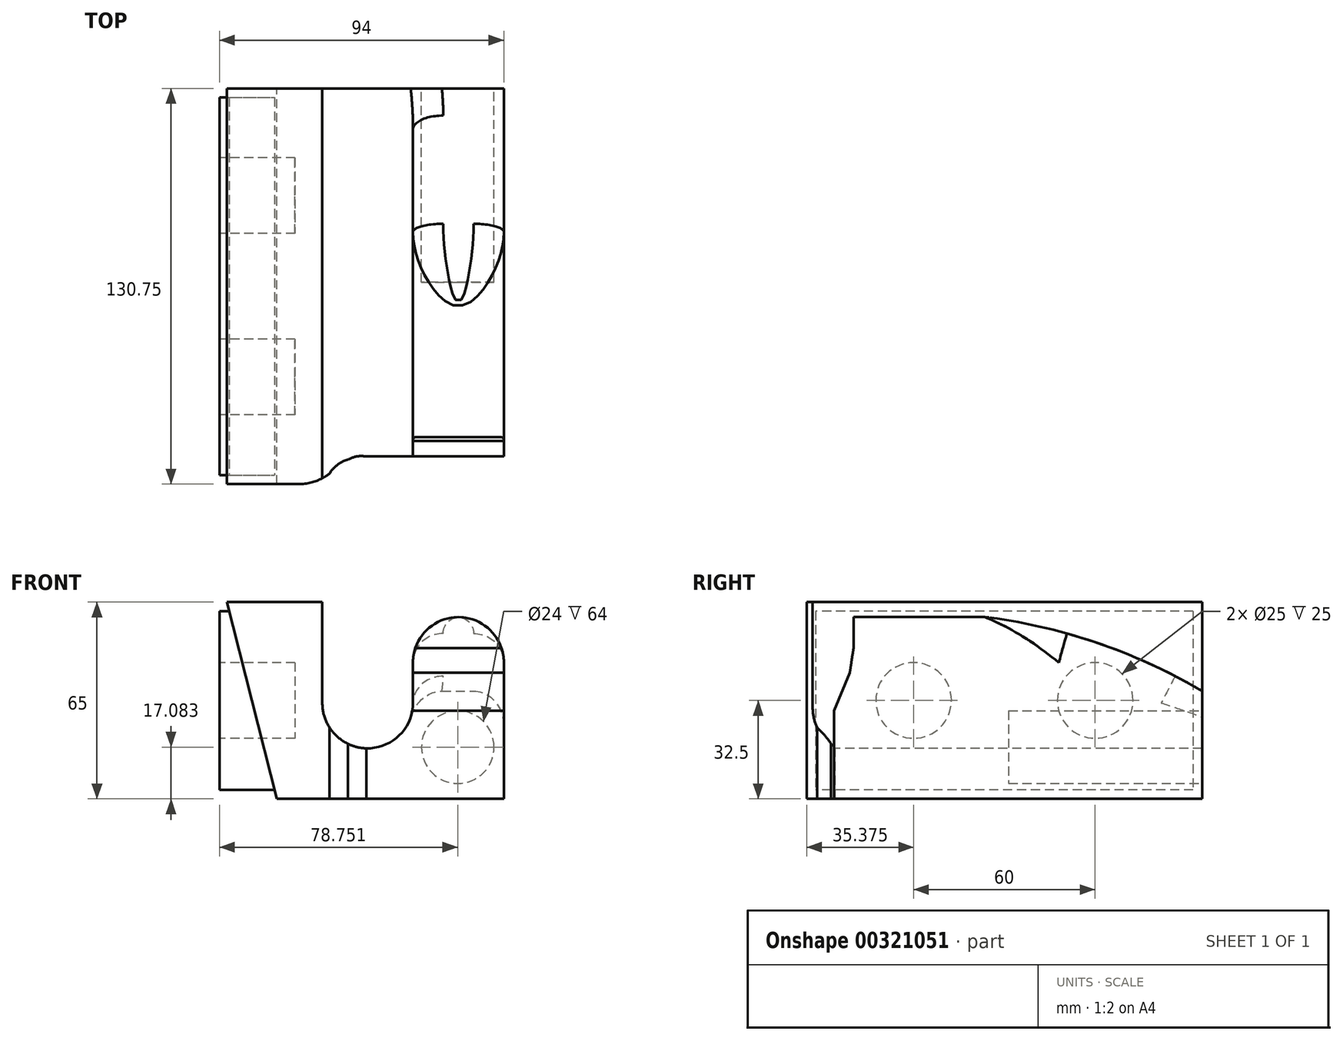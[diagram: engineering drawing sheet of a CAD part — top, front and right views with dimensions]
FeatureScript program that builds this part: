
annotation { "Feature Type Name" : "Feature", "Feature Type Description" : "" }
export const myFeature = defineFeature(function(context is Context, id is Id, definition is map)
    precondition{}
    {
        {
            var Q0;
            Q0=qCreatedBy(makeId("Front.planeOp"),FACE);
            var sketch = newSketch(context, id + "F0", { "sketchPlane" : qUnion([Q0])});
            skLineSegment(sketch, "E0.bottom", {"start": v(37.5, 32.5) * mm, "end": v(-37.5, 32.5) * mm});
            skLineSegment(sketch, "E0.top", {"start": v(37.5, -32.5) * mm, "end": v(-37.5, -32.5) * mm});
            skLineSegment(sketch, "E0.left", {"start": v(37.5, 32.5) * mm, "end": v(37.5, -32.5) * mm});
            skLineSegment(sketch, "E0.right", {"start": v(-37.5, 32.5) * mm, "end": v(-37.5, -32.5) * mm});
            skPoint(sketch, "E0.middle", {"position": v(0, 0) * mm});
            skLineSegment(sketch, "E1", {"start": v(-37.5, 32.5) * mm, "end": v(-54.03, 32.5) * mm});
            skLineSegment(sketch, "E2", {"start": v(-54.03, 32.5) * mm, "end": v(-37.5, -32.5) * mm});
            skSolve(sketch);
        }
        {
            var Q0;
            Q0 = qSketchRegion(id + "F0", true);
            extrude(context, id + "F1", {"entities" : qUnion([Q0]), "depth" : 130.75 * mm});
        }
        {
            var Q0;
            Q0=makeQuery(id+"F1.opExtrude","CAP_FACE",FACE,{"disambiguationData":[OSD([sQuery(id+"F0.wireOp",EDGE,"E0.bottom"),sQuery(id+"F0.wireOp",EDGE,"E0.top"),sQuery(id+"F0.wireOp",EDGE,"E0.left"),sQuery(id+"F0.wireOp",EDGE,"E1"),sQuery(id+"F0.wireOp",EDGE,"E2")])],"isStart":false});
            var sketch = newSketch(context, id + "F2", { "sketchPlane" : qUnion([Q0])});
            skLineSegment(sketch, "E3", {"start": v(37.5, -32.5) * mm, "end": v(37.5, 12.5) * mm});
            skArc(sketch, "E4", {"start": v(37.5, 12.5) * mm, "mid": v(22.47, 27.53) * mm, "end": v(7.45, 12.5) * mm});
            skLineSegment(sketch, "E5", {"start": v(7.45, 12.5) * mm, "end": v(7.45, -0.85) * mm});
            skArc(sketch, "E6", {"start": v(-22.5, -0.85) * mm, "mid": v(-7.53, -15.82) * mm, "end": v(7.45, -0.85) * mm});
            skLineSegment(sketch, "E7", {"start": v(-22.5, -0.85) * mm, "end": v(-22.5, 32.5) * mm});
            skLineSegment(sketch, "E8", {"start": v(-22.5, 32.5) * mm, "end": v(37.5, 32.5) * mm});
            skLineSegment(sketch, "E9", {"start": v(37.5, 32.5) * mm, "end": v(37.5, 12.5) * mm});
            skSolve(sketch);
        }
        {
            var Q0;
            Q0 = qSketchRegion(id + "F2", true);
            extrude(context, id + "F3", {"entities" : qUnion([Q0]), "operationType" : NewBodyOperationType.REMOVE, "oppositeDirection" : true, "depth" : 200 * mm});
        }
        {
            var Q0;
            Q0=makeQuery(id+"F1.opExtrude","SWEPT_FACE",FACE,{"disambiguationData":[OSD([sQuery(id+"F0.wireOp",EDGE,"E0.top")])]});
            var sketch = newSketch(context, id + "F4", { "sketchPlane" : qUnion([Q0])});
            skLineSegment(sketch, "E10", {"start": v(-37.5, 130.75) * mm, "end": v(-30.22, 130.75) * mm});
            skArc(sketch, "E11", {"start": v(-20.1, 127.25) * mm, "mid": v(-24.87, 129.85) * mm, "end": v(-30.22, 130.75) * mm});
            skArc(sketch, "E12", {"start": v(-20.1, 127.25) * mm, "mid": v(-17.49, 124.36) * mm, "end": v(-13.98, 122.65) * mm});
            skArc(sketch, "E13", {"start": v(-13.98, 122.65) * mm, "mid": v(-11.07, 121.6) * mm, "end": v(-7.96, 121.63) * mm});
            skLineSegment(sketch, "E14", {"start": v(-7.96, 121.63) * mm, "end": v(37.5, 121.63) * mm});
            skLineSegment(sketch, "E15", {"start": v(37.5, 121.63) * mm, "end": v(37.5, 130.75) * mm});
            skLineSegment(sketch, "E16", {"start": v(37.5, 130.75) * mm, "end": v(-30.22, 130.75) * mm});
            skSolve(sketch);
        }
        {
            var Q0;
            Q0 = qSketchRegion(id + "F4", true);
            extrude(context, id + "F5", {"entities" : qUnion([Q0]), "operationType" : NewBodyOperationType.REMOVE, "oppositeDirection" : true, "depth" : 200 * mm});
        }
        {
            var Q0;
            Q0=makeQuery(id+"F1.opExtrude","SWEPT_FACE",FACE,{"disambiguationData":[OSD([sQuery(id+"F0.wireOp",EDGE,"E0.left")])]});
            var sketch = newSketch(context, id + "F6", { "sketchPlane" : qUnion([Q0])});
            skLineSegment(sketch, "E17", {"start": v(-121.63, -3.42) * mm, "end": v(-116.52, 9.21) * mm});
            skLineSegment(sketch, "E18", {"start": v(-116.52, 9.21) * mm, "end": v(-115.21, 17.34) * mm});
            skLineSegment(sketch, "E19", {"start": v(-115.21, 17.34) * mm, "end": v(-115.21, 28.67) * mm});
            skLineSegment(sketch, "E20", {"start": v(-115.21, 28.67) * mm, "end": v(-121.63, 28.67) * mm});
            skLineSegment(sketch, "E21", {"start": v(-121.63, 28.67) * mm, "end": v(-121.63, -3.42) * mm});
            skSolve(sketch);
        }
        {
            var Q0;
            Q0 = qSketchRegion(id + "F6", true);
            extrude(context, id + "F7", {"entities" : qUnion([Q0]), "operationType" : NewBodyOperationType.REMOVE, "oppositeDirection" : true, "depth" : 34 * mm});
        }
        {
            var Q0;
            Q0=makeQuery(id+"F1.opExtrude","SWEPT_FACE",FACE,{"disambiguationData":[OSD([sQuery(id+"F0.wireOp",EDGE,"E0.left")])]});
            var sketch = newSketch(context, id + "F8", { "sketchPlane" : qUnion([Q0])});
            skArc(sketch, "E22", {"start": v(0, 3.08) * mm, "mid": v(-42.78, 21.58) * mm, "end": v(-88.8, 28.97) * mm});
            skLineSegment(sketch, "E23", {"start": v(0, 3.08) * mm, "end": v(7.52, 3.08) * mm});
            skLineSegment(sketch, "E24", {"start": v(7.52, 3.08) * mm, "end": v(5.36, 33) * mm});
            skLineSegment(sketch, "E25", {"start": v(5.36, 33) * mm, "end": v(-104, 28.9) * mm});
            skLineSegment(sketch, "E26", {"start": v(-104, 28.9) * mm, "end": v(-88.8, 28.97) * mm});
            skSolve(sketch);
        }
        {
            var Q0;
            Q0 = qSketchRegion(id + "F8", true);
            extrude(context, id + "F9", {"entities" : qUnion([Q0]), "operationType" : NewBodyOperationType.REMOVE, "oppositeDirection" : true, "depth" : 36.2 * mm});
        }
        {
            var Q0;
            Q0=makeQuery(id+"F9.boolean.opBoolean","INTERSECT",EDGE,{"derivedFrom":[makeQuery(id+"F3.boolean.opBoolean","COPY",FACE,{"derivedFrom":makeQuery(id+"F3.opExtrude","SWEPT_FACE",FACE,{"disambiguationData":[OSD([sQuery(id+"F2.wireOp",EDGE,"E4")])]})}),makeQuery(id+"F9.opExtrude","SWEPT_FACE",FACE,{"disambiguationData":[OSD([sQuery(id+"F8.wireOp",EDGE,"E22")])]})]});
            fillet(context, id + "F10", {"entities" : qUnion([Q0]), "radius" : 10 * mm, "tangentPropagation" : true, "allowEdgeOverflow" : false});
        }
        {
            var Q0;
            Q0=qCreatedBy(makeId("Right.planeOp"),FACE);
            cPlane(context, id + "F11", {"entities" : qUnion([Q0]), "cplaneType" : CPlaneType.OFFSET, "offset" : 31.5 * mm, "oppositeDirection" : true, "width" : 150 * mm, "height" : 150 * mm});
        }
        {
            var Q0;
            Q0=qCreatedBy(id+"F11.planeOp",FACE);
            var sketch = newSketch(context, id + "F12", { "sketchPlane" : qUnion([Q0])});
            skLineSegment(sketch, "E27.bottom", {"start": v(-3, 29.5) * mm, "end": v(-127.75, 29.5) * mm});
            skLineSegment(sketch, "E27.top", {"start": v(-3, -29.5) * mm, "end": v(-127.75, -29.5) * mm});
            skLineSegment(sketch, "E27.left", {"start": v(-3, 29.5) * mm, "end": v(-3, -29.5) * mm});
            skLineSegment(sketch, "E27.right", {"start": v(-127.75, 29.5) * mm, "end": v(-127.75, -29.5) * mm});
            skSolve(sketch);
        }
        {
            var Q0;
            Q0 = qSketchRegion(id + "F12", true);
            extrude(context, id + "F13", {"entities" : qUnion([Q0]), "operationType" : NewBodyOperationType.ADD, "oppositeDirection" : true, "depth" : 25 * mm});
        }
        {
            var Q0;
            Q0=makeQuery(id+"F13.opExtrude","CAP_FACE",FACE,{"disambiguationData":[OSD([sQuery(id+"F12.wireOp",EDGE,"E27.bottom"),sQuery(id+"F12.wireOp",EDGE,"E27.top"),sQuery(id+"F12.wireOp",EDGE,"E27.left"),sQuery(id+"F12.wireOp",EDGE,"E27.right")])],"isStart":false});
            var sketch = newSketch(context, id + "F14", { "sketchPlane" : qUnion([Q0])});
            skLineSegment(sketch, "E28.bottom", {"start": v(3, 29.5) * mm, "end": v(127.75, 29.5) * mm, "construction": true});
            skLineSegment(sketch, "E28.top", {"start": v(3, -29.5) * mm, "end": v(127.75, -29.5) * mm, "construction": true});
            skLineSegment(sketch, "E28.left", {"start": v(3, 29.5) * mm, "end": v(3, -29.5) * mm, "construction": true});
            skLineSegment(sketch, "E28.right", {"start": v(127.75, 29.5) * mm, "end": v(127.75, -29.5) * mm, "construction": true});
            skLineSegment(sketch, "E29", {"start": v(3, 0) * mm, "end": v(127.75, 0) * mm, "construction": true});
            skCircle(sketch, "E30", {"center": v(35.38, 0) * mm, "radius": 12.5 * mm});
            skCircle(sketch, "E31", {"center": v(95.37, 0) * mm, "radius": 12.5 * mm});
            skSolve(sketch);
        }
        {
            var Q0;
            Q0 = qSketchRegion(id + "F14", true);
            extrude(context, id + "F15", {"entities" : qUnion([Q0]), "operationType" : NewBodyOperationType.REMOVE, "oppositeDirection" : true, "depth" : 25 * mm});
        }
        {
            var Q0;
            Q0=makeQuery(id+"F1.opExtrude","CAP_FACE",FACE,{"disambiguationData":[OSD([sQuery(id+"F0.wireOp",EDGE,"E0.bottom"),sQuery(id+"F0.wireOp",EDGE,"E0.top"),sQuery(id+"F0.wireOp",EDGE,"E0.left"),sQuery(id+"F0.wireOp",EDGE,"E1"),sQuery(id+"F0.wireOp",EDGE,"E2")])],"isStart":true});
            var sketch = newSketch(context, id + "F16", { "sketchPlane" : qUnion([Q0])});
            skCircle(sketch, "E32", {"center": v(-22.25, -15.42) * mm, "radius": 12 * mm});
            skPoint(sketch, "E32.centerSnap0", {"position": v(-22.25, 3.08) * mm});
            skSolve(sketch);
        }
        {
            var Q0;
            Q0 = qSketchRegion(id + "F16", true);
            extrude(context, id + "F17", {"entities" : qUnion([Q0]), "operationType" : NewBodyOperationType.REMOVE, "oppositeDirection" : true, "depth" : 64 * mm});
        }
    });
